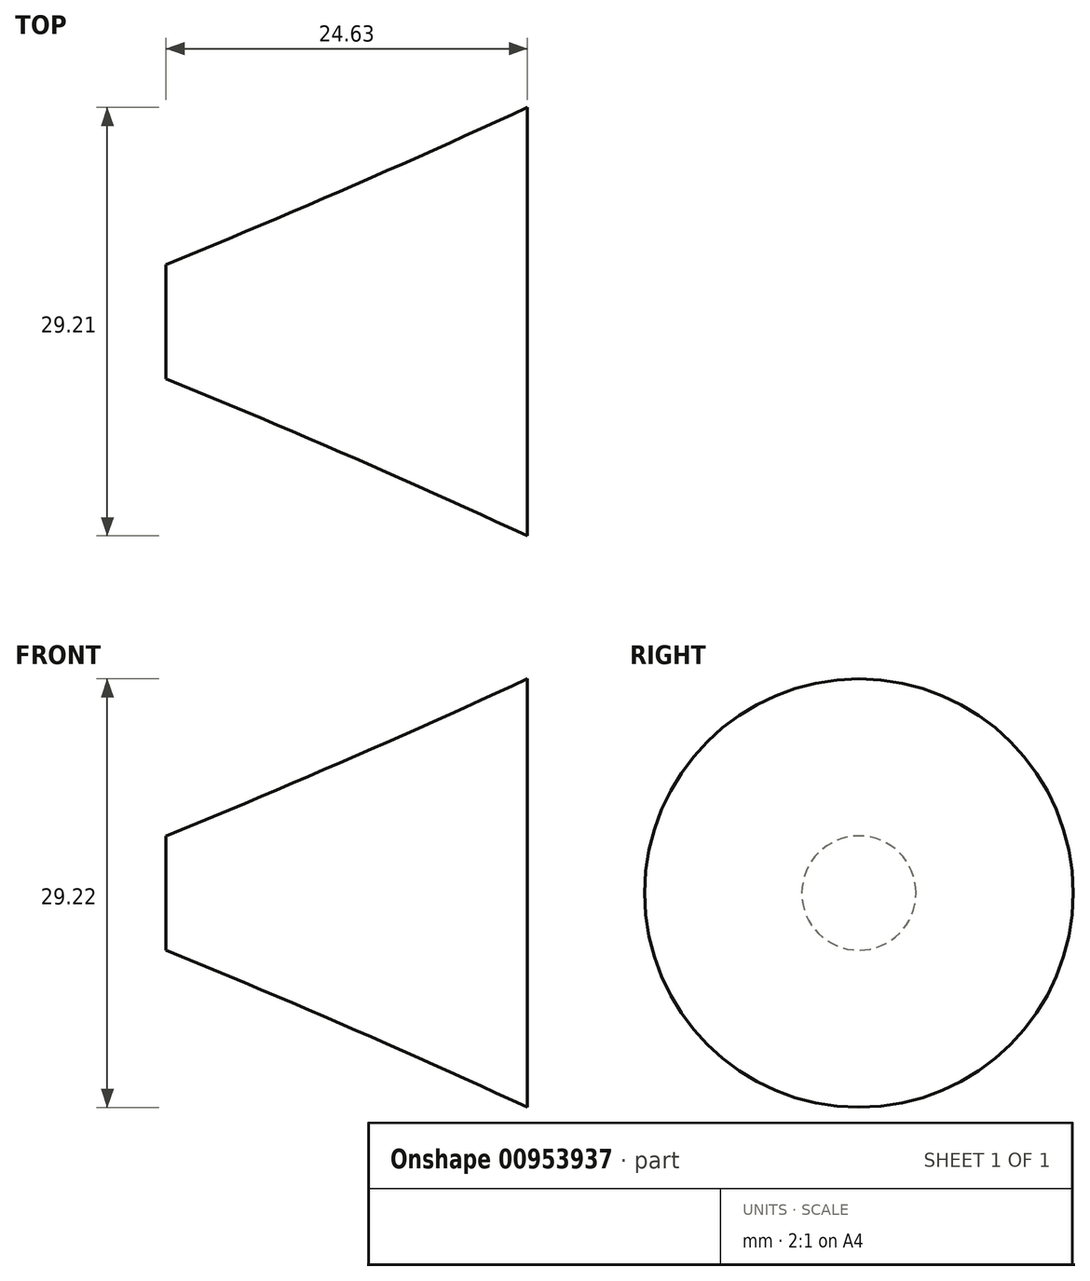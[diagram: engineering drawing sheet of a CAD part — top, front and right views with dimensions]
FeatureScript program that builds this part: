
annotation { "Feature Type Name" : "Feature", "Feature Type Description" : "" }
export const myFeature = defineFeature(function(context is Context, id is Id, definition is map)
    precondition{}
    {
        {
            var Q0;
            Q0=qCreatedBy(makeId("Top.planeOp"),FACE);
            var sketch = newSketch(context, id + "F0", { "sketchPlane" : qUnion([Q0])});
            skLineSegment(sketch, "E0.top", {"start": v(-29.65, 0) * mm, "end": v(-55.88, 0) * mm});
            skLineSegment(sketch, "E0.left", {"start": v(-29.65, 15.85) * mm, "end": v(-29.65, 1.24) * mm});
            skLineSegment(sketch, "E1", {"start": v(-55.88, 1.24) * mm, "end": v(-55.88, 5.14) * mm});
            skLineSegment(sketch, "E2", {"start": v(-31.25, 1.24) * mm, "end": v(-31.25, 15.85) * mm});
            skArc(sketch, "E3", {"start": v(-55.88, 5.14) * mm, "mid": v(-43.5, 10.35) * mm, "end": v(-31.25, 15.85) * mm});
            skLineSegment(sketch, "E4.bottom", {"start": v(-26.62, 15.85) * mm, "end": v(-20.94, 15.85) * mm});
            skLineSegment(sketch, "E4.top", {"start": v(-26.62, -13.36) * mm, "end": v(-20.94, -13.36) * mm});
            skLineSegment(sketch, "E4.left", {"start": v(-26.62, 15.85) * mm, "end": v(-26.62, -13.36) * mm});
            skLineSegment(sketch, "E4.right", {"start": v(-20.94, 15.85) * mm, "end": v(-20.94, -13.36) * mm});
            skLineSegment(sketch, "E5", {"start": v(-26.62, 1.24) * mm, "end": v(-62.69, 1.24) * mm});
            skLineSegment(sketch, "E6.bottom", {"start": v(43.67, 0) * mm, "end": v(46, 0) * mm});
            skLineSegment(sketch, "E6.top", {"start": v(43.67, 1.78) * mm, "end": v(46, 1.78) * mm});
            skLineSegment(sketch, "E6.left", {"start": v(43.67, 0) * mm, "end": v(43.67, 1.78) * mm});
            skLineSegment(sketch, "E6.right", {"start": v(46, 0) * mm, "end": v(46, 1.78) * mm});
            skSolve(sketch);
        }
        {
            var Q0;
            {var subQ0=sQuery(id+"F0.wireOp",EDGE,"E1");Q0=makeQuery(id+"F0.imprint","IMPRINT",FACE,{"disambiguationData":[TD([[makeQuery(id+"F0.imprint","IMPRINT",EDGE,{"derivedFrom":subQ0}),-1.0]])]});}
            var Q1;
            Q1=sQuery(id+"F0.wireOp",EDGE,"E5");
            revolve(context, id + "F1", {"surfaceOperationType" : NewSurfaceOperationType.NEW, "entities" : qUnion([Q0]), "axis" : qUnion([Q1]), "revolveType" : RevolveType.FULL});
        }
    });
